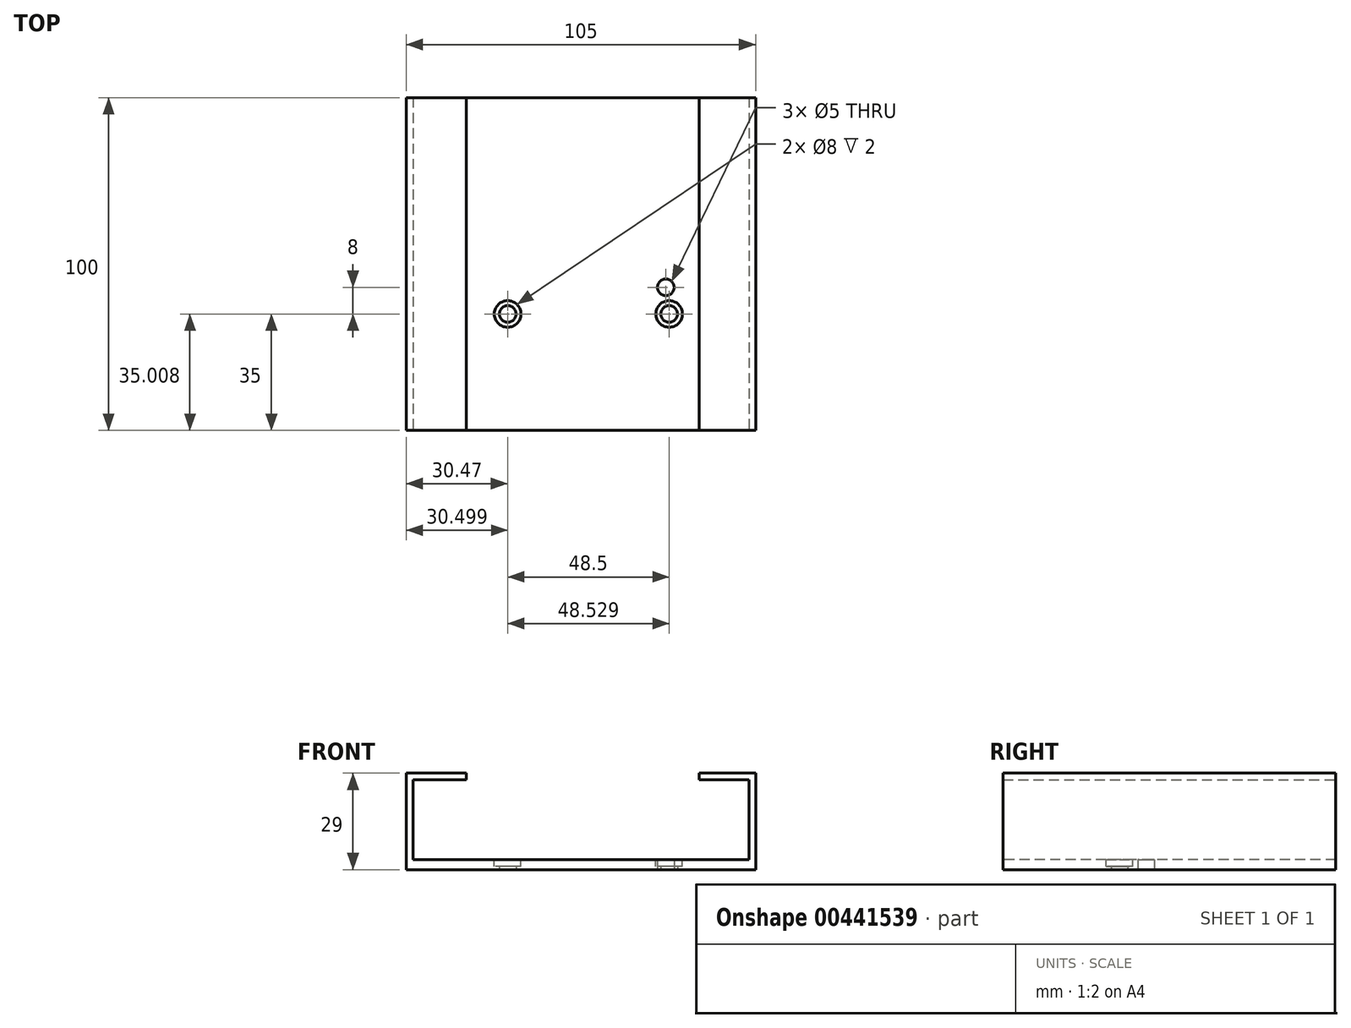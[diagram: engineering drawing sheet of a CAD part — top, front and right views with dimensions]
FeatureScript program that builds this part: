
annotation { "Feature Type Name" : "Feature", "Feature Type Description" : "" }
export const myFeature = defineFeature(function(context is Context, id is Id, definition is map)
    precondition{}
    {
        {
            var Q0;
            Q0=qCreatedBy(makeId("Top.planeOp"),FACE);
            var sketch = newSketch(context, id + "F0", { "sketchPlane" : qUnion([Q0])});
            skLineSegment(sketch, "E0.bottom", {"start": v(-37.07, 22.25) * mm, "end": v(67.93, 22.25) * mm});
            skLineSegment(sketch, "E0.top", {"start": v(-37.07, -77.75) * mm, "end": v(67.93, -77.75) * mm});
            skLineSegment(sketch, "E0.left", {"start": v(-37.07, 22.25) * mm, "end": v(-37.07, -77.75) * mm});
            skLineSegment(sketch, "E0.right", {"start": v(67.93, 22.25) * mm, "end": v(67.93, -77.75) * mm});
            skSolve(sketch);
        }
        {
            var Q0;
            Q0 = qSketchRegion(id + "F0", true);
            extrude(context, id + "F1", {"entities" : qUnion([Q0]), "depth" : 29 * mm});
        }
        {
            var Q0;
            Q0=makeQuery(id+"F1.opExtrude","SWEPT_FACE",FACE,{"disambiguationData":[OSD([sQuery(id+"F0.wireOp",EDGE,"E0.top")])]});
            var sketch = newSketch(context, id + "F2", { "sketchPlane" : qUnion([Q0])});
            skLineSegment(sketch, "E1.bottom", {"start": v(-35.07, 27) * mm, "end": v(65.93, 27) * mm});
            skLineSegment(sketch, "E1.top", {"start": v(-35.07, 3) * mm, "end": v(65.93, 3) * mm});
            skLineSegment(sketch, "E1.left", {"start": v(-35.07, 27) * mm, "end": v(-35.07, 3) * mm});
            skLineSegment(sketch, "E1.right", {"start": v(65.93, 27) * mm, "end": v(65.93, 3) * mm});
            skSolve(sketch);
        }
        {
            var Q0;
            Q0 = qSketchRegion(id + "F2", true);
            extrude(context, id + "F3", {"entities" : qUnion([Q0]), "operationType" : NewBodyOperationType.REMOVE, "oppositeDirection" : true, "depth" : 110 * mm});
        }
        {
            var Q0;
            Q0=makeQuery(id+"F1.opExtrude","CAP_FACE",FACE,{"disambiguationData":[OSD([sQuery(id+"F0.wireOp",EDGE,"E0.bottom"),sQuery(id+"F0.wireOp",EDGE,"E0.top"),sQuery(id+"F0.wireOp",EDGE,"E0.left"),sQuery(id+"F0.wireOp",EDGE,"E0.right")])],"isStart":false});
            var sketch = newSketch(context, id + "F4", { "sketchPlane" : qUnion([Q0])});
            skLineSegment(sketch, "E2.bottom", {"start": v(-19.07, 22.25) * mm, "end": v(50.93, 22.25) * mm});
            skLineSegment(sketch, "E2.top", {"start": v(-19.07, -77.75) * mm, "end": v(50.93, -77.75) * mm});
            skLineSegment(sketch, "E2.left", {"start": v(-19.07, 22.25) * mm, "end": v(-19.07, -77.75) * mm});
            skLineSegment(sketch, "E2.right", {"start": v(50.93, 22.25) * mm, "end": v(50.93, -77.75) * mm});
            skSolve(sketch);
        }
        {
            var Q0;
            Q0=makeQuery(id+"F4.imprint","IMPRINT",FACE,{"disambiguationData":[TD([[makeQuery(id+"F4.imprint","IMPRINT",EDGE,{"derivedFrom":sQuery(id+"F4.wireOp",EDGE,"E2.bottom")}),-1.0]])]});
            extrude(context, id + "F5", {"entities" : qUnion([Q0]), "operationType" : NewBodyOperationType.REMOVE, "oppositeDirection" : true, "depth" : 5 * mm});
        }
        {
            var Q0;
            Q0=qCreatedBy(makeId("Top.planeOp"),FACE);
            var sketch = newSketch(context, id + "F6", { "sketchPlane" : qUnion([Q0])});
            skCircle(sketch, "E3", {"center": v(40.93, -34.75) * mm, "radius": 2.5 * mm});
            skCircle(sketch, "E4", {"center": v(41.93, -42.75) * mm, "radius": 2.5 * mm});
            skCircle(sketch, "E5", {"center": v(-6.57, -42.75) * mm, "radius": 2.5 * mm});
            skCircle(sketch, "E6", {"center": v(41.93, -42.75) * mm, "radius": 4 * mm});
            skCircle(sketch, "E7", {"center": v(-6.57, -42.75) * mm, "radius": 4 * mm});
            skSolve(sketch);
        }
        {
            var Q0;
            Q0=makeQuery(id+"F6.imprint","IMPRINT",FACE,{"disambiguationData":[TD([[makeQuery(id+"F6.imprint","IMPRINT",EDGE,{"derivedFrom":sQuery(id+"F6.wireOp",EDGE,"E3")}),1.0]])]});
            var Q1;
            Q1=makeQuery(id+"F6.imprint","IMPRINT",FACE,{"disambiguationData":[TD([[makeQuery(id+"F6.imprint","IMPRINT",EDGE,{"derivedFrom":sQuery(id+"F6.wireOp",EDGE,"E4")}),1.0]])]});
            var Q2;
            Q2=makeQuery(id+"F6.imprint","IMPRINT",FACE,{"disambiguationData":[TD([[makeQuery(id+"F6.imprint","IMPRINT",EDGE,{"derivedFrom":sQuery(id+"F6.wireOp",EDGE,"E5")}),1.0]])]});
            extrude(context, id + "F7", {"entities" : qUnion([Q0, Q1, Q2]), "operationType" : NewBodyOperationType.REMOVE, "depth" : 5 * mm});
        }
        {
            var Q0;
            Q0=makeQuery(id+"F7.boolean.opBoolean","SPLIT",FACE,{"disambiguationData":[TD([makeQuery(id+"F1.opExtrude","SWEPT_FACE",FACE,{"disambiguationData":[OSD([sQuery(id+"F0.wireOp",EDGE,"E0.bottom")])]})])],"derivedFrom":makeQuery(id+"F3.boolean.opBoolean","COPY",FACE,{"derivedFrom":makeQuery(id+"F3.opExtrude","SWEPT_FACE",FACE,{"disambiguationData":[OSD([sQuery(id+"F2.wireOp",EDGE,"E1.top")])]})})});
            var sketch = newSketch(context, id + "F8", { "sketchPlane" : qUnion([Q0])});
            skCircle(sketch, "E8", {"center": v(41.93, -42.74) * mm, "radius": 4 * mm});
            skCircle(sketch, "E9", {"center": v(-6.6, -42.74) * mm, "radius": 4 * mm});
            skSolve(sketch);
        }
        {
            var Q0;
            Q0 = qSketchRegion(id + "F8", true);
            extrude(context, id + "F9", {"entities" : qUnion([Q0]), "operationType" : NewBodyOperationType.REMOVE, "oppositeDirection" : true, "depth" : 2 * mm});
        }
    });
